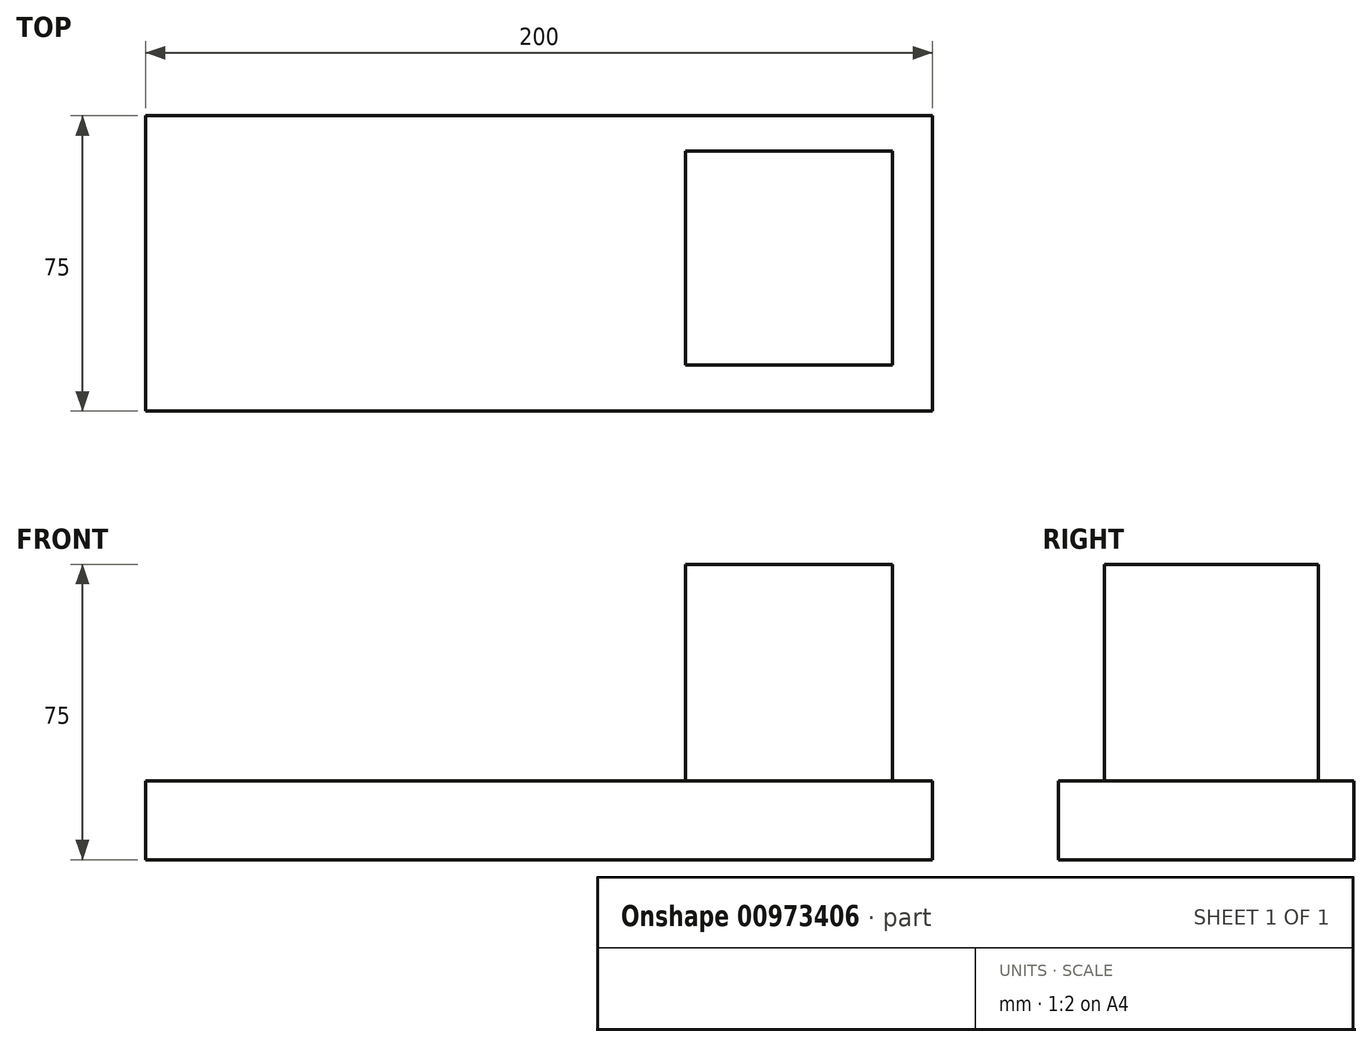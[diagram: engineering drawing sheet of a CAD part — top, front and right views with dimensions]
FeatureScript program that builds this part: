
annotation { "Feature Type Name" : "Feature", "Feature Type Description" : "" }
export const myFeature = defineFeature(function(context is Context, id is Id, definition is map)
    precondition{}
    {
        {
            var Q0;
            Q0=qCreatedBy(makeId("Front.planeOp"),FACE);
            var sketch = newSketch(context, id + "F0", { "sketchPlane" : qUnion([Q0])});
            skLineSegment(sketch, "E0.bottom", {"start": v(-60.38, -2.85) * mm, "end": v(139.62, -2.85) * mm});
            skLineSegment(sketch, "E0.top", {"start": v(-60.38, -22.85) * mm, "end": v(139.62, -22.85) * mm});
            skLineSegment(sketch, "E0.left", {"start": v(-60.38, -2.85) * mm, "end": v(-60.38, -22.85) * mm});
            skLineSegment(sketch, "E0.right", {"start": v(139.62, -2.85) * mm, "end": v(139.62, -22.85) * mm});
            skSolve(sketch);
        }
        {
            var Q0;
            Q0=makeQuery(id+"F0.imprint","IMPRINT",FACE,{"disambiguationData":[TD([[makeQuery(id+"F0.imprint","IMPRINT",EDGE,{"derivedFrom":sQuery(id+"F0.wireOp",EDGE,"E0.bottom")}),-1.0]])]});
            var Q1;
            Q1 = qSketchRegion(id + "F2", true);
            extrude(context, id + "F1", {"entities" : qUnion([Q0, Q1]), "depth" : 75 * mm, "offsetDistance" : 25 * mm});
        }
        {
            var Q0;
            Q0=makeQuery(id+"F1.opExtrude","SWEPT_FACE",FACE,{"disambiguationData":[OSD([sQuery(id+"F0.wireOp",EDGE,"E0.bottom")])]});
            var sketch = newSketch(context, id + "F2", { "sketchPlane" : qUnion([Q0])});
            skLineSegment(sketch, "E1.bottom", {"start": v(129.4, -8.98) * mm, "end": v(76.8, -8.98) * mm});
            skLineSegment(sketch, "E1.top", {"start": v(129.4, -63.36) * mm, "end": v(76.8, -63.36) * mm});
            skLineSegment(sketch, "E1.left", {"start": v(129.4, -8.98) * mm, "end": v(129.4, -63.36) * mm});
            skLineSegment(sketch, "E1.right", {"start": v(76.8, -8.98) * mm, "end": v(76.8, -63.36) * mm});
            skSolve(sketch);
        }
        {
            var Q0;
            Q0 = qSketchRegion(id + "F2", true);
            extrude(context, id + "F3", {"entities" : qUnion([Q0]), "operationType" : NewBodyOperationType.ADD, "depth" : 55 * mm, "offsetDistance" : 25 * mm});
        }
    });
